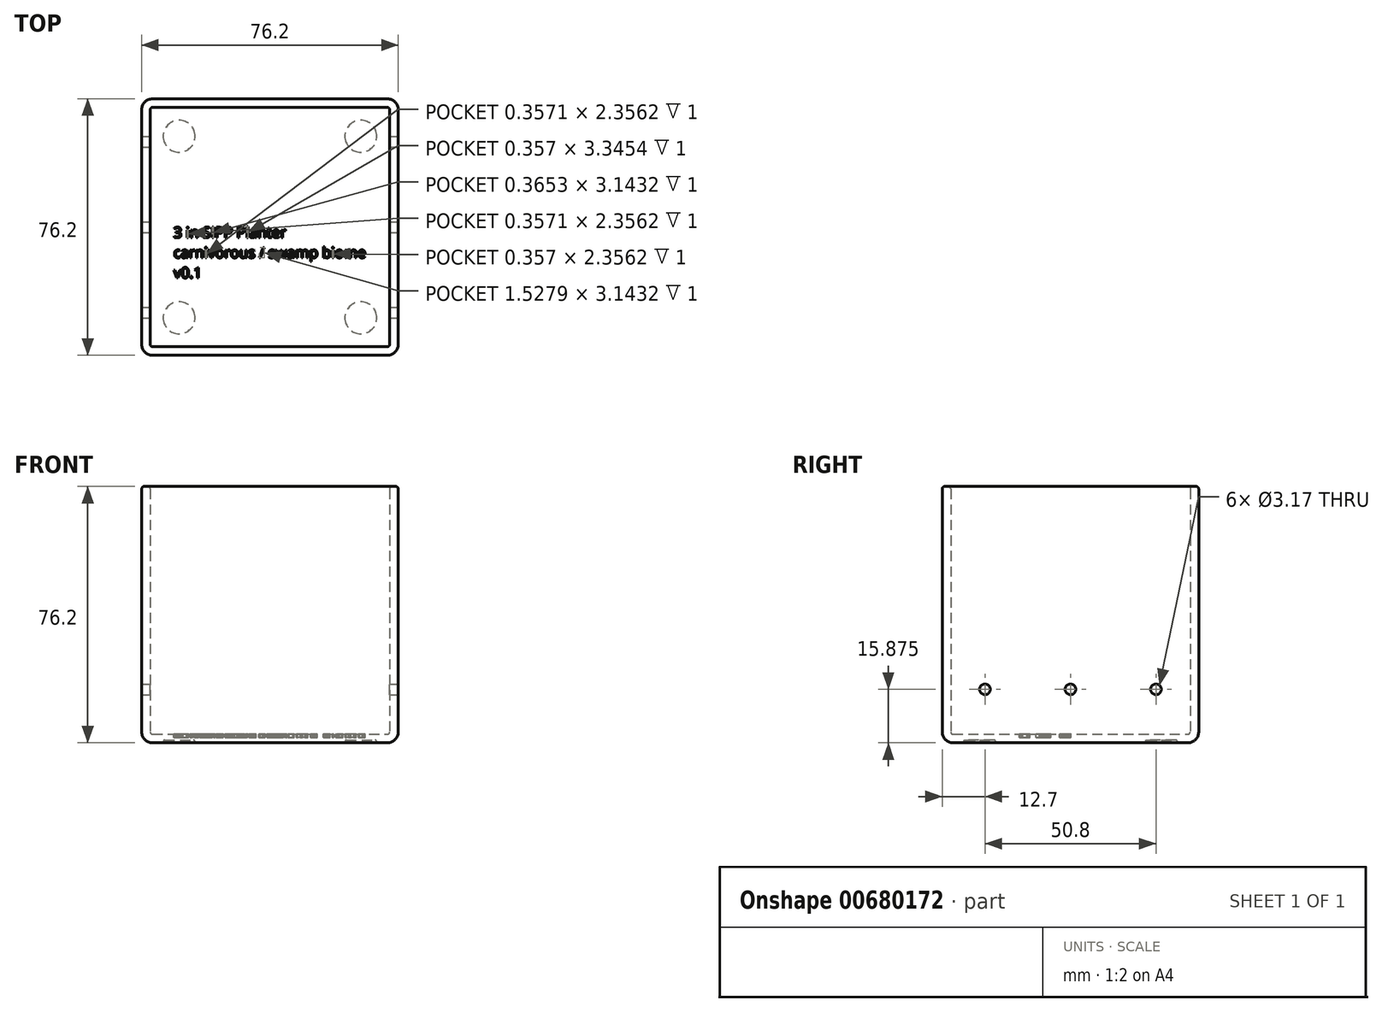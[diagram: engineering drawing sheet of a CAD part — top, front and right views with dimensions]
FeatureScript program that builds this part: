
annotation { "Feature Type Name" : "Feature", "Feature Type Description" : "" }
export const myFeature = defineFeature(function(context is Context, id is Id, definition is map)
    precondition{}
    {
        {
            var Q0;
            Q0=qCreatedBy(makeId("Top.planeOp"),FACE);
            var sketch = newSketch(context, id + "F0", { "sketchPlane" : qUnion([Q0])});
            skLineSegment(sketch, "E0.bottom", {"start": v(73.02, 76.2) * mm, "end": v(3.17, 76.2) * mm});
            skLineSegment(sketch, "E0.top", {"start": v(73.03, 0) * mm, "end": v(3.17, 0) * mm});
            skLineSegment(sketch, "E0.left", {"start": v(76.2, 73.03) * mm, "end": v(76.2, 3.18) * mm});
            skLineSegment(sketch, "E0.right", {"start": v(0, 73.02) * mm, "end": v(0, 3.17) * mm});
            skPoint(sketch, "E1.visualSharp", {"position": v(0, 76.2) * mm});
            skPoint(sketch, "E2.visualSharp", {"position": v(76.2, 76.2) * mm});
            skArc(sketch, "E3.filletArc", {"start": v(3.17, 76.2) * mm, "mid": v(0.93, 75.27) * mm, "end": v(0, 73.02) * mm});
            skArc(sketch, "E4.filletArc", {"start": v(76.2, 73.02) * mm, "mid": v(75.27, 75.27) * mm, "end": v(73.03, 76.2) * mm});
            skPoint(sketch, "E5.visualSharp", {"position": v(76.2, 0) * mm});
            skArc(sketch, "E5.filletArc", {"start": v(73.03, 0) * mm, "mid": v(75.27, 0.93) * mm, "end": v(76.2, 3.18) * mm});
            skPoint(sketch, "E6.visualSharp", {"position": v(0, 0) * mm});
            skArc(sketch, "E6.filletArc", {"start": v(0, 3.17) * mm, "mid": v(0.93, 0.93) * mm, "end": v(3.17, 0) * mm});
            skArc(sketch, "E7.filletArc", {"start": v(76.2, 73.03) * mm, "mid": v(75.27, 75.27) * mm, "end": v(73.02, 76.2) * mm});
            skSolve(sketch);
        }
        {
            var Q0;
            Q0 = qSketchRegion(id + "F0", true);
            extrude(context, id + "F1", {"entities" : qUnion([Q0]), "depth" : 76.2 * mm, "offsetDistance" : 25.4 * mm});
        }
        {
            var Q0;
            Q0=makeQuery(id+"F1.opExtrude","CAP_FACE",FACE,{"disambiguationData":[OSD([sQuery(id+"F0.wireOp",EDGE,"E0.bottom"),sQuery(id+"F0.wireOp",EDGE,"E0.top"),sQuery(id+"F0.wireOp",EDGE,"E0.left"),sQuery(id+"F0.wireOp",EDGE,"E0.right"),sQuery(id+"F0.wireOp",EDGE,"E3.filletArc"),sQuery(id+"F0.wireOp",EDGE,"E5.filletArc"),sQuery(id+"F0.wireOp",EDGE,"E6.filletArc"),sQuery(id+"F0.wireOp",EDGE,"E7.filletArc")])],"isStart":true});
            fillet(context, id + "F2", {"entities" : qUnion([Q0]), "radius" : 3.17 * mm, "tangentPropagation" : true, "allowEdgeOverflow" : false});
        }
        {
            var Q0;
            Q0=makeQuery(id+"F1.opExtrude","CAP_FACE",FACE,{"disambiguationData":[OSD([sQuery(id+"F0.wireOp",EDGE,"E0.bottom"),sQuery(id+"F0.wireOp",EDGE,"E0.top"),sQuery(id+"F0.wireOp",EDGE,"E0.left"),sQuery(id+"F0.wireOp",EDGE,"E0.right"),sQuery(id+"F0.wireOp",EDGE,"E3.filletArc"),sQuery(id+"F0.wireOp",EDGE,"E5.filletArc"),sQuery(id+"F0.wireOp",EDGE,"E6.filletArc"),sQuery(id+"F0.wireOp",EDGE,"E7.filletArc")])],"isStart":false});
            shell(context, id + "F3", {"entities" : qUnion([Q0]), "thickness" : 2.54 * mm});
        }
        {
            var Q0;
            Q0=makeQuery(id+"F1.opExtrude","SWEPT_FACE",FACE,{"disambiguationData":[OSD([sQuery(id+"F0.wireOp",EDGE,"E0.left")])]});
            var sketch = newSketch(context, id + "F4", { "sketchPlane" : qUnion([Q0])});
            skLineSegment(sketch, "E8", {"start": v(3.17, 15.87) * mm, "end": v(73.02, 15.88) * mm, "construction": true});
            skCircle(sketch, "E9", {"center": v(12.7, 15.88) * mm, "radius": 1.59 * mm});
            skCircle(sketch, "E10.1.0.0", {"center": v(38.1, 15.88) * mm, "radius": 1.59 * mm});
            skCircle(sketch, "E10.2.0.0", {"center": v(63.5, 15.88) * mm, "radius": 1.59 * mm});
            skLineSegment(sketch, "E10.direction1", {"start": v(12.7, 15.87) * mm, "end": v(38.1, 15.87) * mm, "construction": true});
            skLineSegment(sketch, "E11", {"start": v(12.7, 15.87) * mm, "end": v(3.17, 15.87) * mm, "construction": true});
            skLineSegment(sketch, "E12", {"start": v(63.5, 15.87) * mm, "end": v(73.02, 15.88) * mm, "construction": true});
            skSolve(sketch);
        }
        {
            var Q0;
            Q0 = qSketchRegion(id + "F4", true);
            extrude(context, id + "F5", {"entities" : qUnion([Q0]), "operationType" : NewBodyOperationType.REMOVE, "endBound" : BoundingType.THROUGH_ALL, "oppositeDirection" : true, "depth" : 25.4 * mm, "offsetDistance" : 25.4 * mm});
        }
        {
            var Q0;
            Q0=makeQuery(id+"F3.opShell","OFFSET_FACE",FACE,{"disambiguationData":[OSD([sQuery(id+"F0.wireOp",EDGE,"E0.bottom"),sQuery(id+"F0.wireOp",EDGE,"E0.top"),sQuery(id+"F0.wireOp",EDGE,"E0.left"),sQuery(id+"F0.wireOp",EDGE,"E0.right"),sQuery(id+"F0.wireOp",EDGE,"E3.filletArc"),sQuery(id+"F0.wireOp",EDGE,"E5.filletArc"),sQuery(id+"F0.wireOp",EDGE,"E6.filletArc"),sQuery(id+"F0.wireOp",EDGE,"E7.filletArc")])]});
            var sketch = newSketch(context, id + "F6", { "sketchPlane" : qUnion([Q0])});
            skText(sketch, "E13", { "text": "3 in SIPP Planter\ncarnivorous / swamp biome\nv0.1", "fontName": "OpenSans-Regular.ttf"});
            skLineSegment(sketch, "E14", {"start": v(38.1, 73.02) * mm, "end": v(38.1, 3.17) * mm, "construction": true});
            const initialGuessF6  = {"E13": [0.00946, 0.03492, 1, 0, 0.00317]};
            skSetInitialGuess(sketch, initialGuessF6);
            skSolve(sketch);
        }
        {
            var Q0;
            Q0 = qSketchRegion(id + "F6", true);
            extrude(context, id + "F7", {"entities" : qUnion([Q0]), "operationType" : NewBodyOperationType.REMOVE, "oppositeDirection" : true, "depth" : 1 * mm, "offsetDistance" : 25.4 * mm});
        }
        {
            var Q0;
            Q0=makeQuery(id+"F1.opExtrude","CAP_FACE",FACE,{"disambiguationData":[OSD([sQuery(id+"F0.wireOp",EDGE,"E0.bottom"),sQuery(id+"F0.wireOp",EDGE,"E0.top"),sQuery(id+"F0.wireOp",EDGE,"E0.left"),sQuery(id+"F0.wireOp",EDGE,"E0.right"),sQuery(id+"F0.wireOp",EDGE,"E3.filletArc"),sQuery(id+"F0.wireOp",EDGE,"E5.filletArc"),sQuery(id+"F0.wireOp",EDGE,"E6.filletArc"),sQuery(id+"F0.wireOp",EDGE,"E7.filletArc")])],"isStart":true});
            var sketch = newSketch(context, id + "F8", { "sketchPlane" : qUnion([Q0])});
            skLineSegment(sketch, "E15", {"start": v(38.1, -3.17) * mm, "end": v(38.1, -73.02) * mm, "construction": true});
            skCircle(sketch, "E16", {"center": v(11.11, -11.11) * mm, "radius": 4.76 * mm});
            skLineSegment(sketch, "E17", {"start": v(11.11, -3.17) * mm, "end": v(11.11, -11.11) * mm, "construction": true});
            skLineSegment(sketch, "E18", {"start": v(11.11, -11.11) * mm, "end": v(3.17, -11.11) * mm, "construction": true});
            skPoint(sketch, "E19", {"position": v(11.11, -6.35) * mm});
            skCircle(sketch, "E20.MirrorC", {"center": v(65.09, -11.11) * mm, "radius": 4.76 * mm});
            skLineSegment(sketch, "E21", {"start": v(3.17, -38.1) * mm, "end": v(73.03, -38.1) * mm, "construction": true});
            skCircle(sketch, "E22.MirrorC", {"center": v(11.11, -65.09) * mm, "radius": 4.76 * mm});
            skCircle(sketch, "E23.MirrorC", {"center": v(65.09, -65.09) * mm, "radius": 4.76 * mm});
            skSolve(sketch);
        }
        {
            var Q0;
            Q0 = qSketchRegion(id + "F8", true);
            extrude(context, id + "F9", {"entities" : qUnion([Q0]), "operationType" : NewBodyOperationType.REMOVE, "oppositeDirection" : true, "depth" : 0.8 * mm, "offsetDistance" : 25.4 * mm, "hasDraft" : true, "draftAngle" : 10 * degree, "draftPullDirection" : true});
        }
        {
            var Q0;
            Q0=makeQuery(id+"F9.boolean.opBoolean","COPY",EDGE,{"derivedFrom":makeQuery(id+"F9.opExtrude","CAP_EDGE",EDGE,{"disambiguationData":[OSD([sQuery(id+"F8.wireOp",EDGE,"E16")])],"isStart":true})});
            var Q1;
            Q1=makeQuery(id+"F9.boolean.opBoolean","COPY",EDGE,{"derivedFrom":makeQuery(id+"F9.opExtrude","CAP_EDGE",EDGE,{"disambiguationData":[OSD([sQuery(id+"F8.wireOp",EDGE,"E22.MirrorC")])],"isStart":true})});
            var Q2;
            Q2=makeQuery(id+"F9.boolean.opBoolean","COPY",EDGE,{"derivedFrom":makeQuery(id+"F9.opExtrude","CAP_EDGE",EDGE,{"disambiguationData":[OSD([sQuery(id+"F8.wireOp",EDGE,"E20.MirrorC")])],"isStart":true})});
            var Q3;
            Q3=makeQuery(id+"F9.boolean.opBoolean","COPY",EDGE,{"derivedFrom":makeQuery(id+"F9.opExtrude","CAP_EDGE",EDGE,{"disambiguationData":[OSD([sQuery(id+"F8.wireOp",EDGE,"E23.MirrorC")])],"isStart":true})});
            var Q4;
            Q4=makeQuery(id+"F9.boolean.opBoolean","COPY",EDGE,{"derivedFrom":makeQuery(id+"F9.opExtrude","CAP_EDGE",EDGE,{"disambiguationData":[OSD([sQuery(id+"F8.wireOp",EDGE,"E23.MirrorC")])],"isStart":false})});
            var Q5;
            Q5=makeQuery(id+"F9.boolean.opBoolean","COPY",EDGE,{"derivedFrom":makeQuery(id+"F9.opExtrude","CAP_EDGE",EDGE,{"disambiguationData":[OSD([sQuery(id+"F8.wireOp",EDGE,"E20.MirrorC")])],"isStart":false})});
            var Q6;
            Q6=makeQuery(id+"F9.boolean.opBoolean","COPY",EDGE,{"derivedFrom":makeQuery(id+"F9.opExtrude","CAP_EDGE",EDGE,{"disambiguationData":[OSD([sQuery(id+"F8.wireOp",EDGE,"E16")])],"isStart":false})});
            var Q7;
            Q7=makeQuery(id+"F9.boolean.opBoolean","COPY",EDGE,{"derivedFrom":makeQuery(id+"F9.opExtrude","CAP_EDGE",EDGE,{"disambiguationData":[OSD([sQuery(id+"F8.wireOp",EDGE,"E22.MirrorC")])],"isStart":false})});
            fillet(context, id + "F10", {"entities" : qUnion([Q0, Q1, Q2, Q3, Q4, Q5, Q6, Q7]), "radius" : 0.4 * mm, "tangentPropagation" : true, "allowEdgeOverflow" : false});
        }
        {
            var Q0;
            Q0=makeQuery(id+"F1.opExtrude","CAP_FACE",FACE,{"disambiguationData":[OSD([sQuery(id+"F0.wireOp",EDGE,"E0.bottom"),sQuery(id+"F0.wireOp",EDGE,"E0.top"),sQuery(id+"F0.wireOp",EDGE,"E0.left"),sQuery(id+"F0.wireOp",EDGE,"E0.right"),sQuery(id+"F0.wireOp",EDGE,"E3.filletArc"),sQuery(id+"F0.wireOp",EDGE,"E5.filletArc"),sQuery(id+"F0.wireOp",EDGE,"E6.filletArc"),sQuery(id+"F0.wireOp",EDGE,"E7.filletArc")])],"isStart":false});
            fillet(context, id + "F11", {"entities" : qUnion([Q0]), "radius" : 0.8 * mm, "tangentPropagation" : true, "allowEdgeOverflow" : false});
        }
    });
